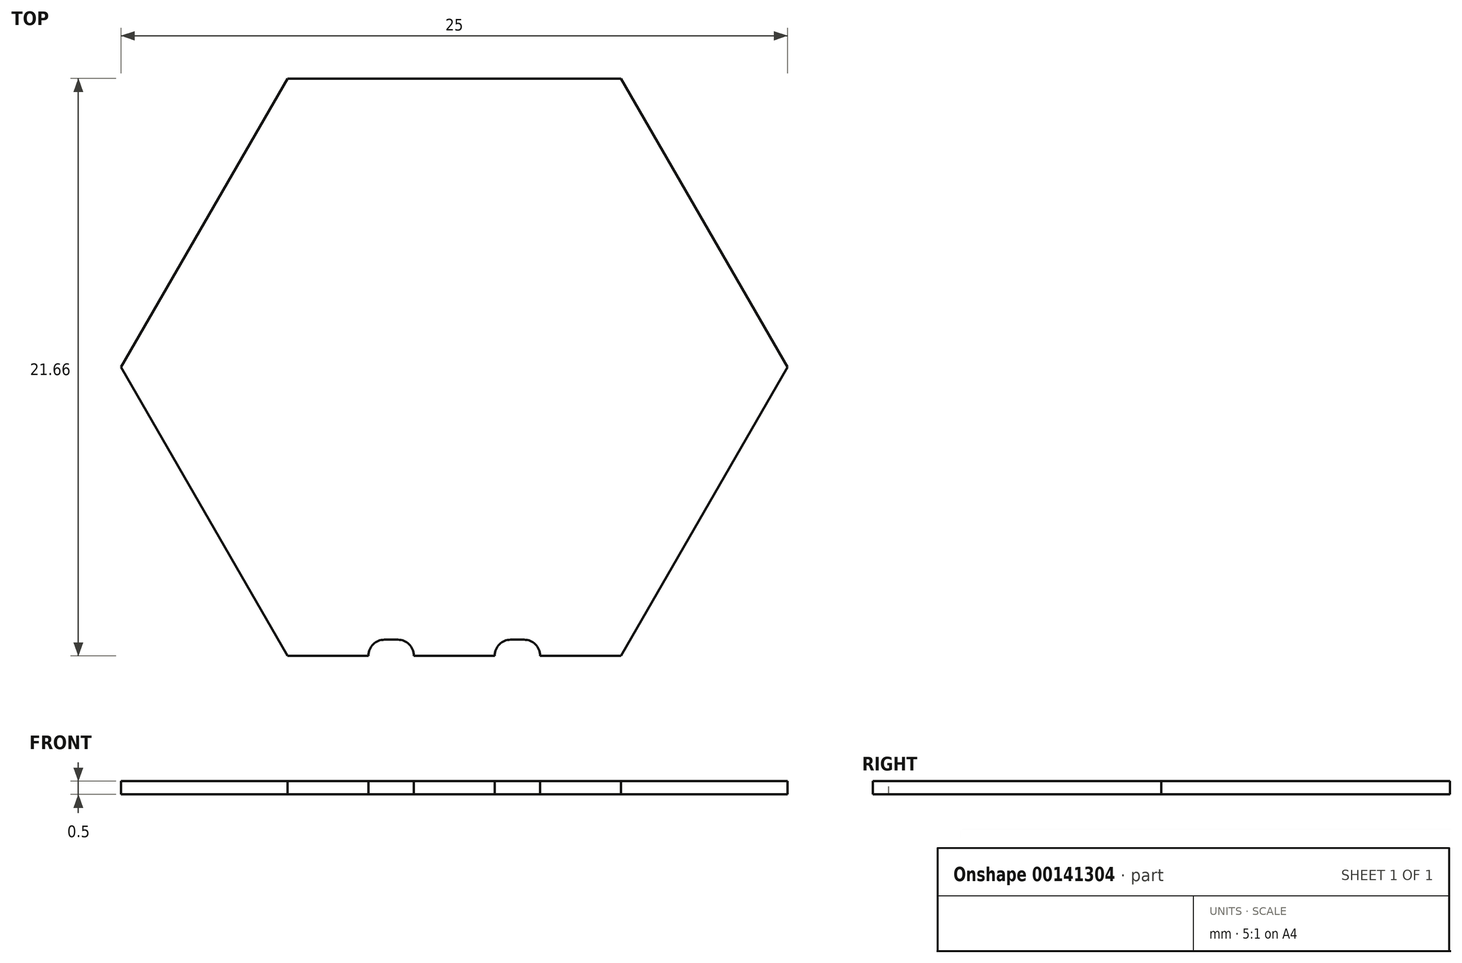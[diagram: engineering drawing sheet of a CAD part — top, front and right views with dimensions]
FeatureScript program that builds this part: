
annotation { "Feature Type Name" : "Feature", "Feature Type Description" : "" }
export const myFeature = defineFeature(function(context is Context, id is Id, definition is map)
    precondition{}
    {
        {
            var Q0;
            Q0=qCreatedBy(makeId("Top.planeOp"),FACE);
            var sketch = newSketch(context, id + "F0", { "sketchPlane" : qUnion([Q0])});
            skCircle(sketch, "E0.cCircle", {"center": v(0, 0) * mm, "radius": 12.5 * mm, "construction": true});
            skLineSegment(sketch, "E0.0", {"start": v(12.5, 0) * mm, "end": v(6.25, -10.83) * mm});
            skLineSegment(sketch, "E0.1", {"start": v(6.25, -10.83) * mm, "end": v(-6.25, -10.83) * mm});
            skLineSegment(sketch, "E0.2", {"start": v(-6.25, -10.83) * mm, "end": v(-12.5, 0) * mm});
            skLineSegment(sketch, "E0.3", {"start": v(-12.5, 0) * mm, "end": v(-6.25, 10.83) * mm});
            skLineSegment(sketch, "E0.4", {"start": v(-6.25, 10.83) * mm, "end": v(6.25, 10.83) * mm});
            skLineSegment(sketch, "E0.5", {"start": v(6.25, 10.83) * mm, "end": v(12.5, 0) * mm});
            skSolve(sketch);
        }
        {
            var Q0;
            Q0=qSketchRegion(id+"F0",true);
            extrude(context, id + "F1", {"entities" : qUnion([Q0]), "depth" : 0.5 * mm});
        }
        {
            var Q0;
            Q0=makeQuery(id+"F1.opExtrude","CAP_FACE",FACE,{"disambiguationData":[OSD([sQuery(id+"F0.wireOp",EDGE,"E0.0"),sQuery(id+"F0.wireOp",EDGE,"E0.1"),sQuery(id+"F0.wireOp",EDGE,"E0.2"),sQuery(id+"F0.wireOp",EDGE,"E0.3"),sQuery(id+"F0.wireOp",EDGE,"E0.4"),sQuery(id+"F0.wireOp",EDGE,"E0.5")])],"isStart":false});
            var sketch = newSketch(context, id + "F2", { "sketchPlane" : qUnion([Q0])});
            skLineSegment(sketch, "E1", {"start": v(2.62, -10.23) * mm, "end": v(2.12, -10.23) * mm});
            skArc(sketch, "E2", {"start": v(2.12, -10.23) * mm, "mid": v(1.7, -10.4) * mm, "end": v(1.52, -10.83) * mm});
            skArc(sketch, "E3", {"start": v(3.22, -10.83) * mm, "mid": v(3.04, -10.4) * mm, "end": v(2.62, -10.23) * mm});
            skLineSegment(sketch, "E4", {"start": v(1.52, -10.83) * mm, "end": v(3.22, -10.83) * mm});
            skLineSegment(sketch, "E5.MirrorCS", {"start": v(-1.52, -10.83) * mm, "end": v(-3.22, -10.83) * mm});
            skArc(sketch, "E6.MirrorCS", {"start": v(-3.22, -10.83) * mm, "mid": v(-3.04, -10.4) * mm, "end": v(-2.62, -10.23) * mm});
            skArc(sketch, "E7.MirrorCS", {"start": v(-2.12, -10.23) * mm, "mid": v(-1.7, -10.4) * mm, "end": v(-1.52, -10.83) * mm});
            skLineSegment(sketch, "E8.MirrorCS", {"start": v(-2.62, -10.23) * mm, "end": v(-2.12, -10.23) * mm});
            skLineSegment(sketch, "E9", {"start": v(-6.25, -10.83) * mm, "end": v(-3.22, -10.83) * mm, "construction": true});
            skLineSegment(sketch, "E10", {"start": v(-1.52, -10.83) * mm, "end": v(1.52, -10.83) * mm, "construction": true});
            skLineSegment(sketch, "E11", {"start": v(3.22, -10.83) * mm, "end": v(6.25, -10.83) * mm, "construction": true});
            skSolve(sketch);
        }
        {
            var Q0;
            Q0 = qSketchRegion(id + "F2", true);
            extrude(context, id + "F3", {"entities" : qUnion([Q0]), "operationType" : NewBodyOperationType.REMOVE, "endBound" : BoundingType.THROUGH_ALL, "oppositeDirection" : true, "depth" : 25 * mm});
        }
    });
